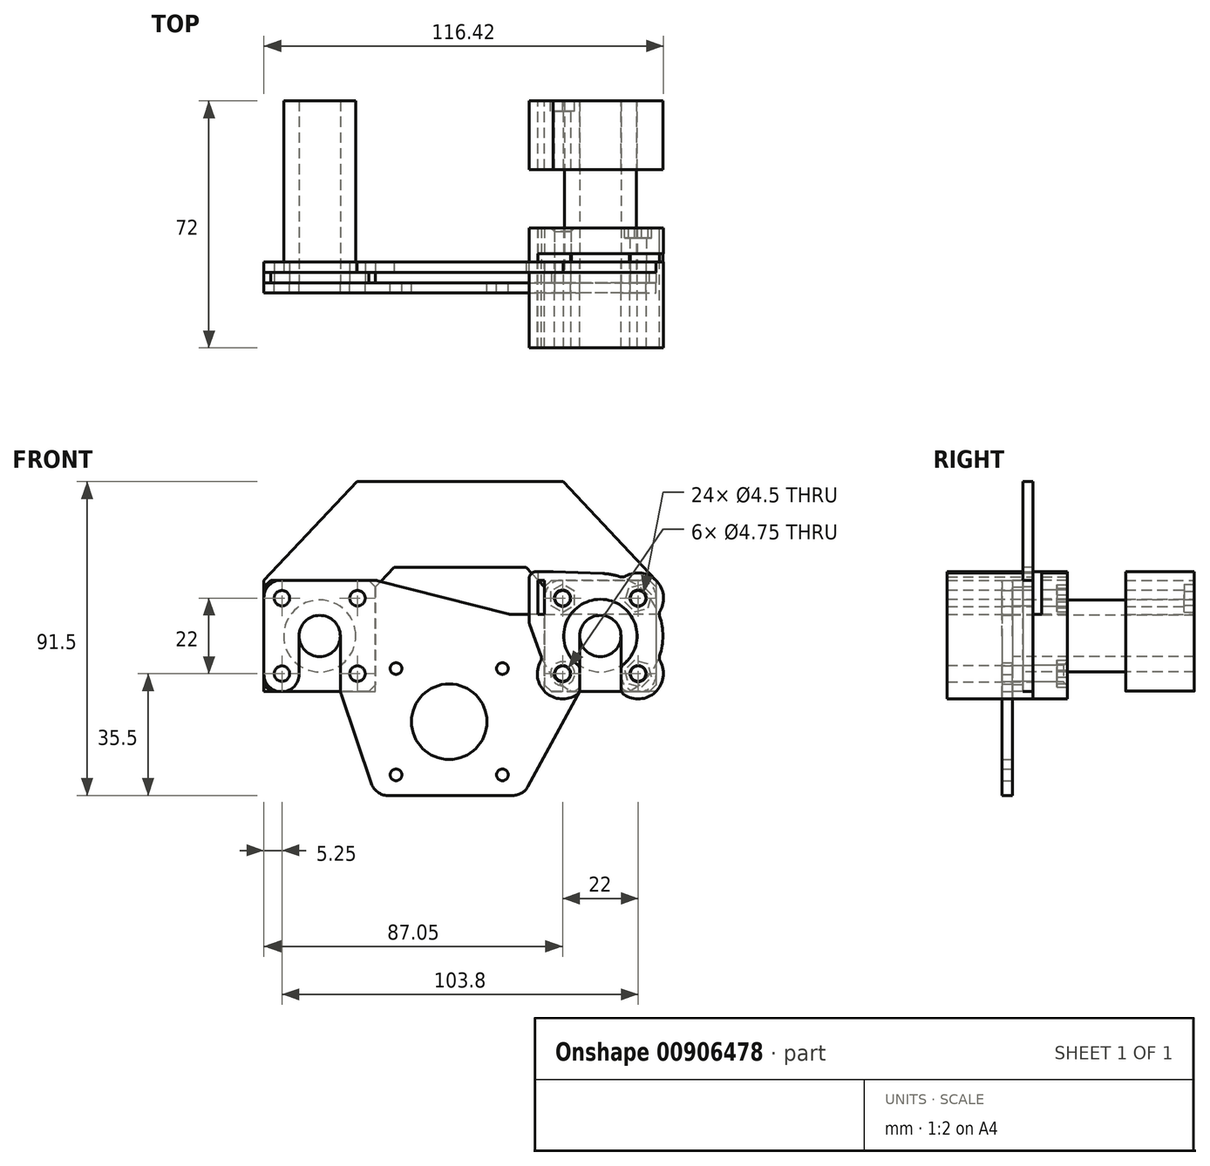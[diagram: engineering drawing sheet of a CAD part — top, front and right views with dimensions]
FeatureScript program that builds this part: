
annotation { "Feature Type Name" : "Feature", "Feature Type Description" : "" }
export const myFeature = defineFeature(function(context is Context, id is Id, definition is map)
    precondition{}
    {
        {
            var Q0;
            Q0=qCreatedBy(makeId("Front.planeOp"),FACE);
            var sketch = newSketch(context, id + "F0", { "sketchPlane" : qUnion([Q0])});
            skLineSegment(sketch, "E0", {"start": v(0, 0) * mm, "end": v(0, 38.28) * mm, "construction": true});
            skLineSegment(sketch, "E1", {"start": v(-57.15, 16.25) * mm, "end": v(-57.15, -16.25) * mm});
            skLineSegment(sketch, "E2", {"start": v(-57.15, -16.25) * mm, "end": v(-46.9, -16.25) * mm});
            skArc(sketch, "E3", {"start": v(-34.9, 0) * mm, "mid": v(-40.9, 6) * mm, "end": v(-46.9, 0) * mm});
            skLineSegment(sketch, "E4.bottom", {"start": v(-29.9, 11) * mm, "end": v(-51.9, 11) * mm, "construction": true});
            skLineSegment(sketch, "E4.top", {"start": v(-29.9, -11) * mm, "end": v(-51.9, -11) * mm, "construction": true});
            skLineSegment(sketch, "E4.left", {"start": v(-29.9, 11) * mm, "end": v(-29.9, -11) * mm, "construction": true});
            skLineSegment(sketch, "E4.right", {"start": v(-51.9, 11) * mm, "end": v(-51.9, -11) * mm, "construction": true});
            skCircle(sketch, "E5", {"center": v(-29.9, 11) * mm, "radius": 2.25 * mm});
            skCircle(sketch, "E6", {"center": v(-29.9, -11) * mm, "radius": 2.25 * mm});
            skCircle(sketch, "E7", {"center": v(-51.9, -11) * mm, "radius": 2.25 * mm});
            skCircle(sketch, "E8", {"center": v(-51.9, 11) * mm, "radius": 2.25 * mm});
            skLineSegment(sketch, "E9.bottom", {"start": v(-57.15, 16.25) * mm, "end": v(-24.65, 16.25) * mm, "construction": true});
            skLineSegment(sketch, "E9.top", {"start": v(-57.15, -16.25) * mm, "end": v(-24.65, -16.25) * mm, "construction": true});
            skLineSegment(sketch, "E9.left", {"start": v(-57.15, 16.25) * mm, "end": v(-57.15, -16.25) * mm, "construction": true});
            skLineSegment(sketch, "E9.right", {"start": v(-24.65, 16.25) * mm, "end": v(-24.65, -16.25) * mm, "construction": true});
            skLineSegment(sketch, "E10", {"start": v(-46.9, 0) * mm, "end": v(-46.9, -16.25) * mm});
            skLineSegment(sketch, "E11", {"start": v(-40.9, 0) * mm, "end": v(-40.9, -16.25) * mm, "construction": true});
            skLineSegment(sketch, "E12.MirrorCS", {"start": v(-34.9, 0) * mm, "end": v(-34.9, -16.25) * mm});
            skCircle(sketch, "E13", {"center": v(-3.15, -25) * mm, "radius": 11 * mm});
            skLineSegment(sketch, "E14.bottom", {"start": v(12.35, -9.5) * mm, "end": v(-18.65, -9.5) * mm, "construction": true});
            skLineSegment(sketch, "E14.top", {"start": v(12.35, -40.5) * mm, "end": v(-18.65, -40.5) * mm, "construction": true});
            skLineSegment(sketch, "E14.left", {"start": v(12.35, -9.5) * mm, "end": v(12.35, -40.5) * mm, "construction": true});
            skLineSegment(sketch, "E14.right", {"start": v(-18.65, -9.5) * mm, "end": v(-18.65, -40.5) * mm, "construction": true});
            skCircle(sketch, "E15", {"center": v(-18.65, -9.5) * mm, "radius": 1.7 * mm});
            skCircle(sketch, "E16", {"center": v(12.35, -9.5) * mm, "radius": 1.7 * mm});
            skCircle(sketch, "E17", {"center": v(12.35, -40.5) * mm, "radius": 1.7 * mm});
            skCircle(sketch, "E18", {"center": v(-18.65, -40.5) * mm, "radius": 1.7 * mm});
            skLineSegment(sketch, "E19.bottom", {"start": v(18.35, -3.5) * mm, "end": v(-24.65, -3.5) * mm, "construction": true});
            skLineSegment(sketch, "E19.top", {"start": v(18.35, -46.5) * mm, "end": v(-24.65, -46.5) * mm, "construction": true});
            skLineSegment(sketch, "E19.left", {"start": v(18.35, -3.5) * mm, "end": v(18.35, -46.5) * mm, "construction": true});
            skLineSegment(sketch, "E19.right", {"start": v(-24.65, -3.5) * mm, "end": v(-24.65, -46.5) * mm, "construction": true});
            skCircle(sketch, "E20.MirrorC", {"center": v(51.9, 11) * mm, "radius": 2.25 * mm});
            skCircle(sketch, "E21.MirrorC", {"center": v(29.9, 11) * mm, "radius": 2.25 * mm});
            skCircle(sketch, "E22.MirrorC", {"center": v(29.9, -11) * mm, "radius": 2.25 * mm});
            skCircle(sketch, "E23.MirrorC", {"center": v(51.9, -11) * mm, "radius": 2.25 * mm});
            skLineSegment(sketch, "E24.MirrorCS", {"start": v(46.9, 0) * mm, "end": v(46.9, -16.25) * mm});
            skLineSegment(sketch, "E25.MirrorCS", {"start": v(34.9, 0) * mm, "end": v(34.9, -16.25) * mm});
            skArc(sketch, "E26.MirrorCS", {"start": v(34.9, 0) * mm, "mid": v(40.9, 6) * mm, "end": v(46.9, 0) * mm});
            skLineSegment(sketch, "E27.MirrorCS", {"start": v(57.15, 16.25) * mm, "end": v(24.65, 16.25) * mm, "construction": true});
            skLineSegment(sketch, "E28.MirrorCS", {"start": v(24.65, 16.25) * mm, "end": v(24.65, -16.25) * mm, "construction": true});
            skLineSegment(sketch, "E29.MirrorCS", {"start": v(57.15, -16.25) * mm, "end": v(24.65, -16.25) * mm, "construction": true});
            skLineSegment(sketch, "E30.MirrorCS", {"start": v(57.15, 16.25) * mm, "end": v(57.15, -16.25) * mm, "construction": true});
            skLineSegment(sketch, "E31", {"start": v(-34.9, -16.25) * mm, "end": v(-24.65, -46.5) * mm});
            skLineSegment(sketch, "E32", {"start": v(18.35, -46.5) * mm, "end": v(-24.65, -46.5) * mm});
            skLineSegment(sketch, "E33", {"start": v(18.35, -46.5) * mm, "end": v(34.9, -16.25) * mm});
            skLineSegment(sketch, "E34", {"start": v(46.9, -16.25) * mm, "end": v(57.15, -16.25) * mm});
            skLineSegment(sketch, "E35", {"start": v(57.15, 16.25) * mm, "end": v(57.15, -16.25) * mm});
            skLineSegment(sketch, "E36", {"start": v(57.15, 16.25) * mm, "end": v(24.65, 16.25) * mm});
            skLineSegment(sketch, "E37", {"start": v(24.65, 16.25) * mm, "end": v(24.65, 6.25) * mm});
            skLineSegment(sketch, "E38", {"start": v(24.65, 6.25) * mm, "end": v(14.65, 6.25) * mm});
            skLineSegment(sketch, "E39", {"start": v(14.65, 6.25) * mm, "end": v(-24.65, 16.25) * mm});
            skLineSegment(sketch, "E40", {"start": v(-57.15, 16.25) * mm, "end": v(-24.65, 16.25) * mm});
            skSolve(sketch);
        }
        {
            var Q0;
            Q0 = qSketchRegion(id + "F0", true);
            extrude(context, id + "F1", {"entities" : qUnion([Q0]), "depth" : 3 * mm, "offsetDistance" : 25 * mm});
        }
        {
            var Q0;
            Q0=makeQuery(id+"F1.opExtrude","SWEPT_EDGE",EDGE,{"disambiguationData":[OSD([sQuery(id+"F0.wireOp",EDGE,"E1"),sQuery(id+"F0.wireOp",EDGE,"E2")])]});
            var Q1;
            Q1=makeQuery(id+"F1.opExtrude","SWEPT_EDGE",EDGE,{"disambiguationData":[OSD([sQuery(id+"F0.wireOp",EDGE,"E1"),sQuery(id+"F0.wireOp",EDGE,"E40")])]});
            var Q2;
            Q2=makeQuery(id+"F1.opExtrude","SWEPT_EDGE",EDGE,{"disambiguationData":[OSD([sQuery(id+"F0.wireOp",EDGE,"E2"),sQuery(id+"F0.wireOp",EDGE,"E10")])]});
            var Q3;
            Q3=makeQuery(id+"F1.opExtrude","SWEPT_EDGE",EDGE,{"disambiguationData":[OSD([sQuery(id+"F0.wireOp",EDGE,"E12.MirrorCS"),sQuery(id+"F0.wireOp",EDGE,"E31")])]});
            var Q4;
            Q4=makeQuery(id+"F1.opExtrude","SWEPT_EDGE",EDGE,{"disambiguationData":[OSD([sQuery(id+"F0.wireOp",EDGE,"E31"),sQuery(id+"F0.wireOp",EDGE,"E32")])]});
            var Q5;
            Q5=makeQuery(id+"F1.opExtrude","SWEPT_EDGE",EDGE,{"disambiguationData":[OSD([sQuery(id+"F0.wireOp",EDGE,"E32"),sQuery(id+"F0.wireOp",EDGE,"E33")])]});
            var Q6;
            Q6=makeQuery(id+"F1.opExtrude","SWEPT_EDGE",EDGE,{"disambiguationData":[OSD([sQuery(id+"F0.wireOp",EDGE,"E25.MirrorCS"),sQuery(id+"F0.wireOp",EDGE,"E33")])]});
            var Q7;
            Q7=makeQuery(id+"F1.opExtrude","SWEPT_EDGE",EDGE,{"disambiguationData":[OSD([sQuery(id+"F0.wireOp",EDGE,"E24.MirrorCS"),sQuery(id+"F0.wireOp",EDGE,"E34")])]});
            var Q8;
            Q8=makeQuery(id+"F1.opExtrude","SWEPT_EDGE",EDGE,{"disambiguationData":[OSD([sQuery(id+"F0.wireOp",EDGE,"E34"),sQuery(id+"F0.wireOp",EDGE,"E35")])]});
            var Q9;
            Q9=makeQuery(id+"F1.opExtrude","SWEPT_EDGE",EDGE,{"disambiguationData":[OSD([sQuery(id+"F0.wireOp",EDGE,"E35"),sQuery(id+"F0.wireOp",EDGE,"E36")])]});
            var Q10;
            Q10=makeQuery(id+"F1.opExtrude","SWEPT_EDGE",EDGE,{"disambiguationData":[OSD([sQuery(id+"F0.wireOp",EDGE,"E36"),sQuery(id+"F0.wireOp",EDGE,"E37")])]});
            var Q11;
            Q11=makeQuery(id+"F1.opExtrude","SWEPT_EDGE",EDGE,{"disambiguationData":[OSD([sQuery(id+"F0.wireOp",EDGE,"E38"),sQuery(id+"F0.wireOp",EDGE,"E39")])]});
            var Q12;
            Q12=makeQuery(id+"F1.opExtrude","SWEPT_EDGE",EDGE,{"disambiguationData":[OSD([sQuery(id+"F0.wireOp",EDGE,"E39"),sQuery(id+"F0.wireOp",EDGE,"E40")])]});
            fillet(context, id + "F2", {"entities" : qUnion([Q0, Q1, Q2, Q3, Q4, Q5, Q6, Q7, Q8, Q9, Q10, Q11, Q12]), "radius" : 5 * mm, "tangentPropagation" : true, "allowEdgeOverflow" : false});
        }
        {
            var Q0;
            Q0=makeQuery(id+"F1.opExtrude","CAP_FACE",FACE,{"disambiguationData":[OSD([sQuery(id+"F0.wireOp",EDGE,"E1"),sQuery(id+"F0.wireOp",EDGE,"E2"),sQuery(id+"F0.wireOp",EDGE,"E3"),sQuery(id+"F0.wireOp",EDGE,"E5"),sQuery(id+"F0.wireOp",EDGE,"E6"),sQuery(id+"F0.wireOp",EDGE,"E7"),sQuery(id+"F0.wireOp",EDGE,"E8"),sQuery(id+"F0.wireOp",EDGE,"E10"),sQuery(id+"F0.wireOp",EDGE,"E12.MirrorCS"),sQuery(id+"F0.wireOp",EDGE,"E13"),sQuery(id+"F0.wireOp",EDGE,"E15"),sQuery(id+"F0.wireOp",EDGE,"E16"),sQuery(id+"F0.wireOp",EDGE,"E17"),sQuery(id+"F0.wireOp",EDGE,"E18"),sQuery(id+"F0.wireOp",EDGE,"E20.MirrorC"),sQuery(id+"F0.wireOp",EDGE,"E21.MirrorC"),sQuery(id+"F0.wireOp",EDGE,"E22.MirrorC"),sQuery(id+"F0.wireOp",EDGE,"E23.MirrorC"),sQuery(id+"F0.wireOp",EDGE,"E24.MirrorCS"),sQuery(id+"F0.wireOp",EDGE,"E25.MirrorCS"),sQuery(id+"F0.wireOp",EDGE,"E26.MirrorCS"),sQuery(id+"F0.wireOp",EDGE,"E31"),sQuery(id+"F0.wireOp",EDGE,"E32"),sQuery(id+"F0.wireOp",EDGE,"E33"),sQuery(id+"F0.wireOp",EDGE,"E34"),sQuery(id+"F0.wireOp",EDGE,"E35"),sQuery(id+"F0.wireOp",EDGE,"E36"),sQuery(id+"F0.wireOp",EDGE,"E37"),sQuery(id+"F0.wireOp",EDGE,"E38"),sQuery(id+"F0.wireOp",EDGE,"E39"),sQuery(id+"F0.wireOp",EDGE,"E40")])],"isStart":true});
            var sketch = newSketch(context, id + "F3", { "sketchPlane" : qUnion([Q0])});
            skLineSegment(sketch, "E41.bottom", {"start": v(-24.65, 16.25) * mm, "end": v(-57.15, 16.25) * mm});
            skLineSegment(sketch, "E41.top", {"start": v(-24.65, -16.25) * mm, "end": v(-57.15, -16.25) * mm});
            skLineSegment(sketch, "E41.left", {"start": v(-24.65, 16.25) * mm, "end": v(-24.65, -16.25) * mm});
            skLineSegment(sketch, "E41.right", {"start": v(-57.15, 16.25) * mm, "end": v(-57.15, -16.25) * mm});
            skPoint(sketch, "E41.middle", {"position": v(-40.9, 0) * mm});
            skCircle(sketch, "E42.0", {"center": v(-51.9, 11) * mm, "radius": 2.25 * mm});
            skCircle(sketch, "E43.0", {"center": v(-29.9, 11) * mm, "radius": 2.25 * mm});
            skCircle(sketch, "E44.0", {"center": v(-29.9, -11) * mm, "radius": 2.25 * mm});
            skCircle(sketch, "E45.0", {"center": v(-51.9, -11) * mm, "radius": 2.25 * mm});
            skCircle(sketch, "E46", {"center": v(-40.9, 0) * mm, "radius": 6 * mm});
            skSolve(sketch);
        }
        {
            var Q0;
            Q0 = qSketchRegion(id + "F3", true);
            extrude(context, id + "F4", {"entities" : qUnion([Q0]), "depth" : 3 * mm, "offsetDistance" : 25 * mm});
        }
        {
            var Q0;
            Q0=makeQuery(id+"F4.opExtrude","CAP_FACE",FACE,{"disambiguationData":[OSD([sQuery(id+"F3.wireOp",EDGE,"E41.bottom"),sQuery(id+"F3.wireOp",EDGE,"E41.top"),sQuery(id+"F3.wireOp",EDGE,"E41.left"),sQuery(id+"F3.wireOp",EDGE,"E41.right"),sQuery(id+"F3.wireOp",EDGE,"E42.0"),sQuery(id+"F3.wireOp",EDGE,"E43.0"),sQuery(id+"F3.wireOp",EDGE,"E44.0"),sQuery(id+"F3.wireOp",EDGE,"E45.0"),sQuery(id+"F3.wireOp",EDGE,"E46")])],"isStart":false});
            var sketch = newSketch(context, id + "F5", { "sketchPlane" : qUnion([Q0])});
            skCircle(sketch, "E47.0", {"center": v(-40.9, 0) * mm, "radius": 6 * mm});
            skCircle(sketch, "E48", {"center": v(-40.9, 0) * mm, "radius": 10.5 * mm});
            skSolve(sketch);
        }
        {
            var Q0;
            Q0 = qSketchRegion(id + "F5", true);
            extrude(context, id + "F6", {"entities" : qUnion([Q0]), "operationType" : NewBodyOperationType.ADD, "depth" : 50 * mm, "offsetDistance" : 25 * mm});
        }
        {
            var Q0;
            Q0=makeQuery(id+"F4.opExtrude","SWEPT_EDGE",EDGE,{"disambiguationData":[OSD([sQuery(id+"F3.wireOp",EDGE,"E41.bottom"),sQuery(id+"F3.wireOp",EDGE,"E41.right")])]});
            var Q1;
            Q1=makeQuery(id+"F4.opExtrude","SWEPT_EDGE",EDGE,{"disambiguationData":[OSD([sQuery(id+"F3.wireOp",EDGE,"E41.bottom"),sQuery(id+"F3.wireOp",EDGE,"E41.left")])]});
            var Q2;
            Q2=makeQuery(id+"F4.opExtrude","SWEPT_EDGE",EDGE,{"disambiguationData":[OSD([sQuery(id+"F3.wireOp",EDGE,"E41.top"),sQuery(id+"F3.wireOp",EDGE,"E41.left")])]});
            var Q3;
            Q3=makeQuery(id+"F4.opExtrude","SWEPT_EDGE",EDGE,{"disambiguationData":[OSD([sQuery(id+"F3.wireOp",EDGE,"E41.top"),sQuery(id+"F3.wireOp",EDGE,"E41.right")])]});
            chamfer(context, id + "F7", {"entities" : qUnion([Q0, Q1, Q2, Q3]), "width" : 2 * mm, "tangentPropagation" : true});
        }
        {
            var Q0;
            Q0=makeQuery(id+"F4.opExtrude","SWEPT_BODY",BODY,{"disambiguationData":[OSD([sQuery(id+"F3.wireOp",EDGE,"E41.bottom"),sQuery(id+"F3.wireOp",EDGE,"E41.top"),sQuery(id+"F3.wireOp",EDGE,"E41.left"),sQuery(id+"F3.wireOp",EDGE,"E41.right"),sQuery(id+"F3.wireOp",EDGE,"E42.0"),sQuery(id+"F3.wireOp",EDGE,"E43.0"),sQuery(id+"F3.wireOp",EDGE,"E44.0"),sQuery(id+"F3.wireOp",EDGE,"E45.0"),sQuery(id+"F3.wireOp",EDGE,"E46")])]});
            var Q1;
            Q1=qCreatedBy(makeId("Right.planeOp"),FACE);
            mirror(context, id + "F8", {"entities" : qUnion([Q0]), "mirrorPlane" : qUnion([Q1])});
        }
        {
            var Q0;
            Q0=makeQuery(id+"F4.opExtrude","CAP_FACE",FACE,{"disambiguationData":[OSD([sQuery(id+"F3.wireOp",EDGE,"E41.bottom"),sQuery(id+"F3.wireOp",EDGE,"E41.top"),sQuery(id+"F3.wireOp",EDGE,"E41.left"),sQuery(id+"F3.wireOp",EDGE,"E41.right"),sQuery(id+"F3.wireOp",EDGE,"E42.0"),sQuery(id+"F3.wireOp",EDGE,"E43.0"),sQuery(id+"F3.wireOp",EDGE,"E44.0"),sQuery(id+"F3.wireOp",EDGE,"E45.0"),sQuery(id+"F3.wireOp",EDGE,"E46")])],"isStart":false});
            cPlane(context, id + "F9", {"entities" : qUnion([Q0]), "cplaneType" : CPlaneType.OFFSET, "offset" : 3 * mm, "width" : 150 * mm, "height" : 150 * mm});
        }
        {
            var Q0;
            Q0=qCreatedBy(id+"F9.planeOp",FACE);
            var sketch = newSketch(context, id + "F10", { "sketchPlane" : qUnion([Q0])});
            skCircle(sketch, "E49.0", {"center": v(-40.9, 0) * mm, "radius": 10.5 * mm, "construction": true});
            skArc(sketch, "E50", {"start": v(-34.9, -8.86) * mm, "mid": v(-40.9, 10.7) * mm, "end": v(-46.9, -8.86) * mm});
            skLineSegment(sketch, "E51", {"start": v(-40.9, 0) * mm, "end": v(-40.9, -10.7) * mm, "construction": true});
            skLineSegment(sketch, "E52", {"start": v(-34.9, -8.86) * mm, "end": v(-34.9, -16.42) * mm});
            skLineSegment(sketch, "E53.MirrorCS", {"start": v(-46.9, -8.86) * mm, "end": v(-46.9, -16.42) * mm});
            skLineSegment(sketch, "E54.bottom", {"start": v(-22.65, 16.25) * mm, "end": v(-24.65, 16.25) * mm});
            skLineSegment(sketch, "E54.top", {"start": v(-22.65, 6.25) * mm, "end": v(-24.65, 6.25) * mm});
            skLineSegment(sketch, "E54.left", {"start": v(-22.65, 16.25) * mm, "end": v(-22.65, 6.25) * mm});
            skLineSegment(sketch, "E54.right", {"start": v(-24.65, 16.25) * mm, "end": v(-24.65, 6.25) * mm});
            skPoint(sketch, "E54.middle", {"position": v(-23.65, 11.25) * mm});
            skArc(sketch, "E55", {"start": v(-23.95, -6.64) * mm, "mid": v(-23.88, -6.44) * mm, "end": v(-23.8, -6.25) * mm});
            skLineSegment(sketch, "E56", {"start": v(-23.8, -6.25) * mm, "end": v(-20.15, 3.75) * mm});
            skLineSegment(sketch, "E57", {"start": v(-20.15, 3.75) * mm, "end": v(-20.15, 18.75) * mm});
            skLineSegment(sketch, "E58", {"start": v(-20.15, 18.75) * mm, "end": v(-27.15, 18.75) * mm});
            skLineSegment(sketch, "E59", {"start": v(-27.15, 18.75) * mm, "end": v(-41.6, 18.19) * mm});
            skLineSegment(sketch, "E60", {"start": v(-22.65, 16.25) * mm, "end": v(-22.65, 18.75) * mm, "construction": true});
            skLineSegment(sketch, "E61", {"start": v(-22.65, 16.25) * mm, "end": v(-20.15, 16.25) * mm, "construction": true});
            skLineSegment(sketch, "E62", {"start": v(-27.15, 18.75) * mm, "end": v(-27.15, 16.25) * mm, "construction": true});
            skArc(sketch, "E63.trimOffspring", {"start": v(-41.6, 18.19) * mm, "mid": v(-44.63, 17.81) * mm, "end": v(-47.54, 16.95) * mm});
            skLineSegment(sketch, "E64", {"start": v(-22.65, 6.25) * mm, "end": v(-22.65, 3.75) * mm, "construction": true});
            skLineSegment(sketch, "E65", {"start": v(-22.65, 3.75) * mm, "end": v(-20.15, 3.75) * mm, "construction": true});
            skCircle(sketch, "E66.0", {"center": v(-51.9, 11) * mm, "radius": 2.38 * mm});
            skCircle(sketch, "E67.0", {"center": v(-29.9, 11) * mm, "radius": 2.38 * mm});
            skCircle(sketch, "E68.0", {"center": v(-29.9, -11) * mm, "radius": 2.38 * mm});
            skCircle(sketch, "E69.0", {"center": v(-51.9, -11) * mm, "radius": 2.38 * mm});
            skArc(sketch, "E70", {"start": v(-47.54, 16.95) * mm, "mid": v(-57.11, 16.21) * mm, "end": v(-57.85, 6.64) * mm});
            skArc(sketch, "E71", {"start": v(-57.85, -6.64) * mm, "mid": v(-56.81, -16.5) * mm, "end": v(-46.9, -16.42) * mm});
            skArc(sketch, "E72", {"start": v(-34.9, -16.42) * mm, "mid": v(-24.99, -16.5) * mm, "end": v(-23.95, -6.64) * mm});
            skArc(sketch, "E73.trimOffspring", {"start": v(-57.85, 6.64) * mm, "mid": v(-59.1, 0) * mm, "end": v(-57.85, -6.64) * mm});
            skPoint(sketch, "E74.orphan", {"position": v(-46.9, -17.18) * mm});
            skPoint(sketch, "E75.orphan", {"position": v(-34.9, -17.18) * mm});
            skLineSegment(sketch, "E76", {"start": v(-27.15, 16.25) * mm, "end": v(-24.65, 16.25) * mm, "construction": true});
            skSolve(sketch);
        }
        {
            var Q0;
            Q0 = qSketchRegion(id + "F10", true);
            extrude(context, id + "F11", {"entities" : qUnion([Q0]), "depth" : 10 * mm, "offsetDistance" : 25 * mm});
        }
        {
            var Q0;
            Q0=makeQuery(id+"F11.opExtrude","SWEPT_FACE",FACE,{"disambiguationData":[OSD([sQuery(id+"F10.wireOp",EDGE,"E54.left")])]});
            var sketch = newSketch(context, id + "F12", { "sketchPlane" : qUnion([Q0])});
            skLineSegment(sketch, "E77.bottom", {"start": v(6, 6.25) * mm, "end": v(8.5, 6.25) * mm});
            skLineSegment(sketch, "E77.top", {"start": v(6, 18.75) * mm, "end": v(8.5, 18.75) * mm});
            skLineSegment(sketch, "E77.left", {"start": v(6, 6.25) * mm, "end": v(6, 18.75) * mm});
            skLineSegment(sketch, "E77.right", {"start": v(8.5, 6.25) * mm, "end": v(8.5, 18.75) * mm});
            skSolve(sketch);
        }
        {
            var Q0;
            Q0=makeQuery(id+"F6.opExtrude","CAP_FACE",FACE,{"disambiguationData":[OSD([sQuery(id+"F5.wireOp",EDGE,"E47.0"),sQuery(id+"F5.wireOp",EDGE,"E48")])],"isStart":false});
            var sketch = newSketch(context, id + "F13", { "sketchPlane" : qUnion([Q0])});
            skArc(sketch, "E78.0.0", {"start": v(-41.6, 18.19) * mm, "mid": v(-44.63, 17.81) * mm, "end": v(-47.54, 16.95) * mm});
            skArc(sketch, "E78.0.2", {"start": v(-57.85, 6.64) * mm, "mid": v(-59.1, 0) * mm, "end": v(-57.85, -6.64) * mm});
            skArc(sketch, "E78.0.3", {"start": v(-47.54, -16.95) * mm, "mid": v(-47.21, -16.7) * mm, "end": v(-46.9, -16.42) * mm});
            skLineSegment(sketch, "E78.0.4", {"start": v(-46.9, -16.42) * mm, "end": v(-46.9, -8.86) * mm});
            skArc(sketch, "E78.0.5", {"start": v(-46.9, -8.86) * mm, "mid": v(-40.9, 10.7) * mm, "end": v(-34.9, -8.86) * mm});
            skLineSegment(sketch, "E78.0.6", {"start": v(-34.9, -8.86) * mm, "end": v(-34.9, -16.42) * mm});
            skArc(sketch, "E78.0.7", {"start": v(-34.9, -16.42) * mm, "mid": v(-34.59, -16.7) * mm, "end": v(-34.26, -16.95) * mm});
            skArc(sketch, "E78.0.8", {"start": v(-23.95, -6.64) * mm, "mid": v(-23.88, -6.44) * mm, "end": v(-23.8, -6.25) * mm});
            skLineSegment(sketch, "E78.0.9", {"start": v(-23.8, -6.25) * mm, "end": v(-20.15, 3.75) * mm});
            skLineSegment(sketch, "E78.0.10", {"start": v(-20.15, 3.75) * mm, "end": v(-20.15, 18.75) * mm});
            skLineSegment(sketch, "E78.0.11", {"start": v(-20.15, 18.75) * mm, "end": v(-27.15, 18.75) * mm});
            skLineSegment(sketch, "E78.0.12", {"start": v(-27.15, 18.75) * mm, "end": v(-41.6, 18.19) * mm});
            skCircle(sketch, "E79.0", {"center": v(-29.9, 11) * mm, "radius": 2.37 * mm});
            skLineSegment(sketch, "E80.0", {"start": v(-24.65, 16.25) * mm, "end": v(-24.65, 6.25) * mm});
            skLineSegment(sketch, "E81.0", {"start": v(-22.65, 16.25) * mm, "end": v(-24.65, 16.25) * mm});
            skLineSegment(sketch, "E82.0", {"start": v(-22.65, 16.25) * mm, "end": v(-22.65, 6.25) * mm});
            skLineSegment(sketch, "E83.0", {"start": v(-22.65, 6.25) * mm, "end": v(-24.65, 6.25) * mm});
            skArc(sketch, "E84", {"start": v(-34.26, -16.95) * mm, "mid": v(-27.89, -12.72) * mm, "end": v(-23.8, -6.25) * mm});
            skArc(sketch, "E85.trimOffspring", {"start": v(-41.6, 18.19) * mm, "mid": v(-58.85, 3.03) * mm, "end": v(-47.54, -16.95) * mm});
            skSolve(sketch);
        }
        {
            var Q0;
            Q0 = qSketchRegion(id + "F13", true);
            extrude(context, id + "F14", {"entities" : qUnion([Q0]), "oppositeDirection" : true, "depth" : 20 * mm, "offsetDistance" : 25 * mm});
        }
        {
            var Q0;
            Q0 = qSketchRegion(id + "F12", true);
            extrude(context, id + "F15", {"entities" : qUnion([Q0]), "operationType" : NewBodyOperationType.REMOVE, "endBound" : BoundingType.THROUGH_ALL, "depth" : 25 * mm, "offsetDistance" : 25 * mm});
        }
        {
            var Q0;
            Q0=makeQuery(id+"F11.opExtrude","CAP_FACE",FACE,{"disambiguationData":[OSD([sQuery(id+"F10.wireOp",EDGE,"E50"),sQuery(id+"F10.wireOp",EDGE,"E52"),sQuery(id+"F10.wireOp",EDGE,"E53.MirrorCS"),sQuery(id+"F10.wireOp",EDGE,"E54.bottom"),sQuery(id+"F10.wireOp",EDGE,"E54.top"),sQuery(id+"F10.wireOp",EDGE,"E54.left"),sQuery(id+"F10.wireOp",EDGE,"E54.right"),sQuery(id+"F10.wireOp",EDGE,"E55"),sQuery(id+"F10.wireOp",EDGE,"E56"),sQuery(id+"F10.wireOp",EDGE,"E57"),sQuery(id+"F10.wireOp",EDGE,"E58"),sQuery(id+"F10.wireOp",EDGE,"E59"),sQuery(id+"F10.wireOp",EDGE,"E63.trimOffspring"),sQuery(id+"F10.wireOp",EDGE,"E66.0"),sQuery(id+"F10.wireOp",EDGE,"E67.0"),sQuery(id+"F10.wireOp",EDGE,"E68.0"),sQuery(id+"F10.wireOp",EDGE,"E69.0"),sQuery(id+"F10.wireOp",EDGE,"E70"),sQuery(id+"F10.wireOp",EDGE,"E71"),sQuery(id+"F10.wireOp",EDGE,"E72"),sQuery(id+"F10.wireOp",EDGE,"E73.trimOffspring")])],"isStart":false});
            var sketch = newSketch(context, id + "F16", { "sketchPlane" : qUnion([Q0])});
            skCircle(sketch, "E86.cCircle", {"center": v(-51.9, 11) * mm, "radius": 3.5 * mm, "construction": true});
            skLineSegment(sketch, "E86.0", {"start": v(-49.04, 13.86) * mm, "end": v(-48, 9.95) * mm});
            skLineSegment(sketch, "E86.1", {"start": v(-48, 9.95) * mm, "end": v(-50.85, 7.1) * mm});
            skLineSegment(sketch, "E86.2", {"start": v(-50.85, 7.1) * mm, "end": v(-54.76, 8.14) * mm});
            skLineSegment(sketch, "E86.3", {"start": v(-54.76, 8.14) * mm, "end": v(-55.8, 12.05) * mm});
            skLineSegment(sketch, "E86.4", {"start": v(-55.8, 12.05) * mm, "end": v(-52.95, 14.9) * mm});
            skLineSegment(sketch, "E86.5", {"start": v(-52.95, 14.9) * mm, "end": v(-49.04, 13.86) * mm});
            skPoint(sketch, "E86.0.midPoint", {"position": v(-48.52, 11.9) * mm});
            skCircle(sketch, "E87.cCircle", {"center": v(-51.9, -11) * mm, "radius": 3.5 * mm, "construction": true});
            skLineSegment(sketch, "E87.0", {"start": v(-54.76, -8.14) * mm, "end": v(-50.85, -7.1) * mm});
            skLineSegment(sketch, "E87.1", {"start": v(-50.85, -7.1) * mm, "end": v(-48, -9.95) * mm});
            skLineSegment(sketch, "E87.2", {"start": v(-48, -9.95) * mm, "end": v(-49.04, -13.86) * mm});
            skLineSegment(sketch, "E87.3", {"start": v(-49.04, -13.86) * mm, "end": v(-52.95, -14.9) * mm});
            skLineSegment(sketch, "E87.4", {"start": v(-52.95, -14.9) * mm, "end": v(-55.8, -12.05) * mm});
            skLineSegment(sketch, "E87.5", {"start": v(-55.8, -12.05) * mm, "end": v(-54.76, -8.14) * mm});
            skPoint(sketch, "E87.0.midPoint", {"position": v(-52.8, -7.62) * mm});
            skCircle(sketch, "E88.cCircle", {"center": v(-29.9, -11) * mm, "radius": 3.5 * mm, "construction": true});
            skLineSegment(sketch, "E88.0", {"start": v(-27.04, -8.14) * mm, "end": v(-26, -12.05) * mm, "construction": true});
            skLineSegment(sketch, "E88.1", {"start": v(-26, -12.05) * mm, "end": v(-28.85, -14.9) * mm, "construction": true});
            skLineSegment(sketch, "E88.2", {"start": v(-28.85, -14.9) * mm, "end": v(-32.76, -13.86) * mm, "construction": true});
            skLineSegment(sketch, "E88.3", {"start": v(-32.76, -13.86) * mm, "end": v(-33.8, -9.95) * mm, "construction": true});
            skLineSegment(sketch, "E88.4", {"start": v(-33.8, -9.95) * mm, "end": v(-30.95, -7.1) * mm, "construction": true});
            skLineSegment(sketch, "E88.5", {"start": v(-30.95, -7.1) * mm, "end": v(-27.04, -8.14) * mm, "construction": true});
            skPoint(sketch, "E88.0.midPoint", {"position": v(-26.52, -10.1) * mm});
            skLineSegment(sketch, "E89", {"start": v(-49.43, 8.53) * mm, "end": v(-32.37, -8.53) * mm, "construction": true});
            skSolve(sketch);
        }
        {
            var Q0;
            Q0 = qSketchRegion(id + "F16", true);
            extrude(context, id + "F17", {"entities" : qUnion([Q0]), "operationType" : NewBodyOperationType.REMOVE, "oppositeDirection" : true, "depth" : 3 * mm, "offsetDistance" : 25 * mm});
        }
        {
            var Q0;
            Q0=makeQuery(id+"F14.opExtrude","SWEPT_EDGE",EDGE,{"disambiguationData":[OSD([sQuery(id+"F13.wireOp",EDGE,"E78.0.3"),sQuery(id+"F13.wireOp",EDGE,"E78.0.4")])]});
            var Q1;
            Q1=makeQuery(id+"F11.opExtrude","SWEPT_EDGE",EDGE,{"disambiguationData":[OSD([sQuery(id+"F10.wireOp",EDGE,"E63.trimOffspring"),sQuery(id+"F10.wireOp",EDGE,"E70")])]});
            var Q2;
            Q2=makeQuery(id+"F11.opExtrude","SWEPT_EDGE",EDGE,{"disambiguationData":[OSD([sQuery(id+"F10.wireOp",EDGE,"E70"),sQuery(id+"F10.wireOp",EDGE,"E73.trimOffspring")])]});
            var Q3;
            Q3=makeQuery(id+"F11.opExtrude","SWEPT_EDGE",EDGE,{"disambiguationData":[OSD([sQuery(id+"F10.wireOp",EDGE,"E71"),sQuery(id+"F10.wireOp",EDGE,"E73.trimOffspring")])]});
            var Q4;
            Q4=makeQuery(id+"F11.opExtrude","SWEPT_EDGE",EDGE,{"disambiguationData":[OSD([sQuery(id+"F10.wireOp",EDGE,"E53.MirrorCS"),sQuery(id+"F10.wireOp",EDGE,"E71")])]});
            var Q5;
            Q5=makeQuery(id+"F11.opExtrude","SWEPT_EDGE",EDGE,{"disambiguationData":[OSD([sQuery(id+"F10.wireOp",EDGE,"E50"),sQuery(id+"F10.wireOp",EDGE,"E53.MirrorCS")])]});
            var Q6;
            Q6=makeQuery(id+"F11.opExtrude","SWEPT_EDGE",EDGE,{"disambiguationData":[OSD([sQuery(id+"F10.wireOp",EDGE,"E55"),sQuery(id+"F10.wireOp",EDGE,"E72")])]});
            var Q7;
            Q7=makeQuery(id+"F11.opExtrude","SWEPT_EDGE",EDGE,{"disambiguationData":[OSD([sQuery(id+"F10.wireOp",EDGE,"E56"),sQuery(id+"F10.wireOp",EDGE,"E57")])]});
            var Q8;
            Q8=makeQuery(id+"F11.opExtrude","SWEPT_EDGE",EDGE,{"disambiguationData":[OSD([sQuery(id+"F10.wireOp",EDGE,"E57"),sQuery(id+"F10.wireOp",EDGE,"E58")])]});
            var Q9;
            Q9=makeQuery(id+"F11.opExtrude","SWEPT_EDGE",EDGE,{"disambiguationData":[OSD([sQuery(id+"F10.wireOp",EDGE,"E58"),sQuery(id+"F10.wireOp",EDGE,"E59")])]});
            var Q10;
            Q10=makeQuery(id+"F11.opExtrude","SWEPT_EDGE",EDGE,{"disambiguationData":[OSD([sQuery(id+"F10.wireOp",EDGE,"E50"),sQuery(id+"F10.wireOp",EDGE,"E52")])]});
            var Q11;
            Q11=makeQuery(id+"F11.opExtrude","SWEPT_EDGE",EDGE,{"disambiguationData":[OSD([sQuery(id+"F10.wireOp",EDGE,"E52"),sQuery(id+"F10.wireOp",EDGE,"E72")])]});
            var Q12;
            Q12=makeQuery(id+"F14.opExtrude","SWEPT_EDGE",EDGE,{"disambiguationData":[OSD([sQuery(id+"F13.wireOp",EDGE,"E78.0.4"),sQuery(id+"F13.wireOp",EDGE,"E78.0.5")])]});
            var Q13;
            Q13=makeQuery(id+"F14.opExtrude","SWEPT_EDGE",EDGE,{"disambiguationData":[OSD([sQuery(id+"F13.wireOp",EDGE,"E78.0.7"),sQuery(id+"F13.wireOp",EDGE,"E84")])]});
            var Q14;
            Q14=makeQuery(id+"F14.opExtrude","SWEPT_EDGE",EDGE,{"disambiguationData":[OSD([sQuery(id+"F13.wireOp",EDGE,"E78.0.5"),sQuery(id+"F13.wireOp",EDGE,"E78.0.6")])]});
            var Q15;
            Q15=makeQuery(id+"F14.opExtrude","SWEPT_EDGE",EDGE,{"disambiguationData":[OSD([sQuery(id+"F13.wireOp",EDGE,"E78.0.9"),sQuery(id+"F13.wireOp",EDGE,"E78.0.10")])]});
            var Q16;
            Q16=makeQuery(id+"F14.opExtrude","SWEPT_EDGE",EDGE,{"disambiguationData":[OSD([sQuery(id+"F13.wireOp",EDGE,"E78.0.10"),sQuery(id+"F13.wireOp",EDGE,"E78.0.11")])]});
            fillet(context, id + "F18", {"entities" : qUnion([Q0, Q1, Q2, Q3, Q4, Q5, Q6, Q7, Q8, Q9, Q10, Q11, Q12, Q13, Q14, Q15, Q16]), "radius" : 2 * mm, "tangentPropagation" : true, "allowEdgeOverflow" : false});
        }
        {
            var Q0;
            Q0=makeQuery(id+"F4.opExtrude","CAP_FACE",FACE,{"disambiguationData":[OSD([sQuery(id+"F3.wireOp",EDGE,"E41.bottom"),sQuery(id+"F3.wireOp",EDGE,"E41.top"),sQuery(id+"F3.wireOp",EDGE,"E41.left"),sQuery(id+"F3.wireOp",EDGE,"E41.right"),sQuery(id+"F3.wireOp",EDGE,"E42.0"),sQuery(id+"F3.wireOp",EDGE,"E43.0"),sQuery(id+"F3.wireOp",EDGE,"E44.0"),sQuery(id+"F3.wireOp",EDGE,"E45.0"),sQuery(id+"F3.wireOp",EDGE,"E46")])],"isStart":false});
            var sketch = newSketch(context, id + "F19", { "sketchPlane" : qUnion([Q0])});
            skCircle(sketch, "E90.0", {"center": v(-51.9, 11) * mm, "radius": 2.25 * mm});
            skCircle(sketch, "E91.0", {"center": v(-29.9, 11) * mm, "radius": 2.25 * mm});
            skCircle(sketch, "E92.0", {"center": v(-51.9, -11) * mm, "radius": 2.25 * mm});
            skCircle(sketch, "E93.0", {"center": v(-29.9, -11) * mm, "radius": 2.25 * mm});
            skCircle(sketch, "E94.0", {"center": v(51.9, -11) * mm, "radius": 2.25 * mm});
            skCircle(sketch, "E95.0", {"center": v(29.9, -11) * mm, "radius": 2.25 * mm});
            skCircle(sketch, "E96.0", {"center": v(29.9, 11) * mm, "radius": 2.25 * mm});
            skCircle(sketch, "E97.0", {"center": v(51.9, 11) * mm, "radius": 2.25 * mm});
            skLineSegment(sketch, "E98", {"start": v(-57.15, 16.25) * mm, "end": v(-57.15, -16.25) * mm});
            skLineSegment(sketch, "E99", {"start": v(-57.15, -16.25) * mm, "end": v(-24.65, -16.25) * mm});
            skLineSegment(sketch, "E100", {"start": v(-24.65, -16.25) * mm, "end": v(-24.65, 14.25) * mm});
            skLineSegment(sketch, "E101", {"start": v(0, 0) * mm, "end": v(0, 20) * mm, "construction": true});
            skLineSegment(sketch, "E102", {"start": v(-24.65, 14.25) * mm, "end": v(-19.22, 20) * mm});
            skLineSegment(sketch, "E103", {"start": v(-19.22, 20) * mm, "end": v(0, 20) * mm});
            skLineSegment(sketch, "E104.MirrorCS", {"start": v(19.22, 20) * mm, "end": v(0, 20) * mm});
            skLineSegment(sketch, "E105.MirrorCS", {"start": v(24.65, 14.25) * mm, "end": v(19.22, 20) * mm});
            skLineSegment(sketch, "E106.MirrorCS", {"start": v(24.65, -16.25) * mm, "end": v(24.65, 14.25) * mm});
            skLineSegment(sketch, "E107.MirrorCS", {"start": v(57.15, -16.25) * mm, "end": v(24.65, -16.25) * mm});
            skLineSegment(sketch, "E108.MirrorCS", {"start": v(57.15, 16.25) * mm, "end": v(57.15, -16.25) * mm});
            skLineSegment(sketch, "E109", {"start": v(-57.15, 16.25) * mm, "end": v(-57.15, 16.25) * mm});
            skLineSegment(sketch, "E110", {"start": v(-57.15, 16.25) * mm, "end": v(-30, 45) * mm});
            skLineSegment(sketch, "E111", {"start": v(-30, 45) * mm, "end": v(0, 45) * mm});
            skLineSegment(sketch, "E112.MirrorCS", {"start": v(30, 45) * mm, "end": v(0, 45) * mm});
            skLineSegment(sketch, "E113.MirrorCS", {"start": v(57.15, 16.25) * mm, "end": v(30, 45) * mm});
            skLineSegment(sketch, "E114.MirrorCS", {"start": v(57.15, 16.25) * mm, "end": v(57.15, 16.25) * mm});
            skLineSegment(sketch, "E115", {"start": v(-15.46, 23.98) * mm, "end": v(-33.64, 41.14) * mm, "construction": true});
            skLineSegment(sketch, "E116", {"start": v(0, 20) * mm, "end": v(0, 45) * mm, "construction": true});
            skSolve(sketch);
        }
        {
            var Q0;
            Q0 = qSketchRegion(id + "F19", true);
            extrude(context, id + "F20", {"entities" : qUnion([Q0]), "depth" : 3 * mm, "offsetDistance" : 25 * mm});
        }
        {
            var Q0;
            Q0=makeQuery(id+"F18.opFillet","BLEND_EDGE",EDGE,{"blendedFrom":[makeQuery(id+"F14.opExtrude","SWEPT_EDGE",EDGE,{"disambiguationData":[OSD([sQuery(id+"F13.wireOp",EDGE,"E78.0.7"),sQuery(id+"F13.wireOp",EDGE,"E84")])]}),makeQuery(id+"F14.opExtrude","SWEPT_FACE",FACE,{"disambiguationData":[OSD([sQuery(id+"F13.wireOp",EDGE,"E78.0.6")])]})],"blendedInto":[makeQuery(id+"F14.opExtrude","SWEPT_FACE",FACE,{"disambiguationData":[OSD([sQuery(id+"F13.wireOp",EDGE,"E78.0.6")])]})]});
            var Q1;
            Q1=makeQuery(id+"F18.opFillet","BLEND_EDGE",EDGE,{"blendedFrom":[makeQuery(id+"F14.opExtrude","SWEPT_EDGE",EDGE,{"disambiguationData":[OSD([sQuery(id+"F13.wireOp",EDGE,"E78.0.3"),sQuery(id+"F13.wireOp",EDGE,"E78.0.4")])]}),makeQuery(id+"F14.opExtrude","SWEPT_FACE",FACE,{"disambiguationData":[OSD([sQuery(id+"F13.wireOp",EDGE,"E85.trimOffspring")])]})],"blendedInto":[makeQuery(id+"F14.opExtrude","SWEPT_FACE",FACE,{"disambiguationData":[OSD([sQuery(id+"F13.wireOp",EDGE,"E85.trimOffspring")])]})]});
            fillet(context, id + "F21", {"entities" : qUnion([Q0, Q1]), "radius" : 2 * mm, "tangentPropagation" : true, "allowEdgeOverflow" : false});
        }
        {
            var Q0;
            Q0=makeQuery(id+"F14.opExtrude","CAP_FACE",FACE,{"disambiguationData":[OSD([sQuery(id+"F13.wireOp",EDGE,"E78.0.3"),sQuery(id+"F13.wireOp",EDGE,"E78.0.4"),sQuery(id+"F13.wireOp",EDGE,"E78.0.5"),sQuery(id+"F13.wireOp",EDGE,"E78.0.6"),sQuery(id+"F13.wireOp",EDGE,"E78.0.7"),sQuery(id+"F13.wireOp",EDGE,"E78.0.9"),sQuery(id+"F13.wireOp",EDGE,"E78.0.10"),sQuery(id+"F13.wireOp",EDGE,"E78.0.11"),sQuery(id+"F13.wireOp",EDGE,"E78.0.12"),sQuery(id+"F13.wireOp",EDGE,"E79.0"),sQuery(id+"F13.wireOp",EDGE,"E80.0"),sQuery(id+"F13.wireOp",EDGE,"E81.0"),sQuery(id+"F13.wireOp",EDGE,"E82.0"),sQuery(id+"F13.wireOp",EDGE,"E83.0"),sQuery(id+"F13.wireOp",EDGE,"E84"),sQuery(id+"F13.wireOp",EDGE,"E85.trimOffspring")])],"isStart":true});
            var sketch = newSketch(context, id + "F22", { "sketchPlane" : qUnion([Q0])});
            skCircle(sketch, "E117.cCircle", {"center": v(-29.9, 11) * mm, "radius": 3.5 * mm, "construction": true});
            skLineSegment(sketch, "E117.0", {"start": v(-29.9, 15.04) * mm, "end": v(-26.4, 13.02) * mm});
            skLineSegment(sketch, "E117.1", {"start": v(-26.4, 13.02) * mm, "end": v(-26.4, 8.98) * mm});
            skLineSegment(sketch, "E117.2", {"start": v(-26.4, 8.98) * mm, "end": v(-29.9, 6.96) * mm});
            skLineSegment(sketch, "E117.3", {"start": v(-29.9, 6.96) * mm, "end": v(-33.4, 8.98) * mm});
            skLineSegment(sketch, "E117.4", {"start": v(-33.4, 8.98) * mm, "end": v(-33.4, 13.02) * mm});
            skLineSegment(sketch, "E117.5", {"start": v(-33.4, 13.02) * mm, "end": v(-29.9, 15.04) * mm});
            skPoint(sketch, "E117.0.midPoint", {"position": v(-28.15, 14.03) * mm});
            skSolve(sketch);
        }
        {
            var Q0;
            Q0=makeQuery(id+"F22.imprint","IMPRINT",FACE,{"disambiguationData":[TD([[makeQuery(id+"F22.imprint","IMPRINT",EDGE,{"derivedFrom":sQuery(id+"F22.wireOp",EDGE,"E117.0")}),-1.0]])]});
            extrude(context, id + "F23", {"entities" : qUnion([Q0]), "operationType" : NewBodyOperationType.REMOVE, "oppositeDirection" : true, "depth" : 3 * mm, "offsetDistance" : 25 * mm});
        }
        {
            var Q0;
            Q0=makeQuery(id+"F11.opExtrude","CAP_FACE",FACE,{"disambiguationData":[OSD([sQuery(id+"F10.wireOp",EDGE,"E50"),sQuery(id+"F10.wireOp",EDGE,"E52"),sQuery(id+"F10.wireOp",EDGE,"E53.MirrorCS"),sQuery(id+"F10.wireOp",EDGE,"E54.bottom"),sQuery(id+"F10.wireOp",EDGE,"E54.top"),sQuery(id+"F10.wireOp",EDGE,"E54.left"),sQuery(id+"F10.wireOp",EDGE,"E54.right"),sQuery(id+"F10.wireOp",EDGE,"E55"),sQuery(id+"F10.wireOp",EDGE,"E56"),sQuery(id+"F10.wireOp",EDGE,"E57"),sQuery(id+"F10.wireOp",EDGE,"E58"),sQuery(id+"F10.wireOp",EDGE,"E59"),sQuery(id+"F10.wireOp",EDGE,"E63.trimOffspring"),sQuery(id+"F10.wireOp",EDGE,"E66.0"),sQuery(id+"F10.wireOp",EDGE,"E67.0"),sQuery(id+"F10.wireOp",EDGE,"E68.0"),sQuery(id+"F10.wireOp",EDGE,"E69.0"),sQuery(id+"F10.wireOp",EDGE,"E70"),sQuery(id+"F10.wireOp",EDGE,"E71"),sQuery(id+"F10.wireOp",EDGE,"E72"),sQuery(id+"F10.wireOp",EDGE,"E73.trimOffspring")])],"isStart":false});
            var sketch = newSketch(context, id + "F24", { "sketchPlane" : qUnion([Q0])});
            skCircle(sketch, "E118.0", {"center": v(-29.9, -11) * mm, "radius": 2.37 * mm, "construction": true});
            skCircle(sketch, "E119", {"center": v(-29.9, -11) * mm, "radius": 3.5 * mm});
            skSolve(sketch);
        }
        {
            var Q0;
            Q0 = qSketchRegion(id + "F24", true);
            extrude(context, id + "F25", {"entities" : qUnion([Q0]), "operationType" : NewBodyOperationType.REMOVE, "oppositeDirection" : true, "depth" : 25 * mm, "offsetDistance" : 25 * mm, "hasDraft" : true, "draftAngle" : 45 * degree, "draftPullDirection" : true});
        }
        {
            var Q0;
            {var subQ0=sQuery(id+"F10.wireOp",EDGE,"E58");var subQ1=sQuery(id+"F10.wireOp",EDGE,"E72");var subQ2=sQuery(id+"F10.wireOp",EDGE,"E56");var subQ3=sQuery(id+"F10.wireOp",EDGE,"E55");var subQ5=sQuery(id+"F10.wireOp",EDGE,"E57");var subQ6=sQuery(id+"F10.wireOp",EDGE,"E50");var subQ7=sQuery(id+"F10.wireOp",EDGE,"E52");var subQ8=sQuery(id+"F10.wireOp",EDGE,"E68.0");var subQ9=sQuery(id+"F10.wireOp",EDGE,"E54.top");var subQ10=sQuery(id+"F10.wireOp",EDGE,"E54.left");Q0=makeQuery(id+"F15.boolean.opBoolean","SPLIT",FACE,{"disambiguationData":[TD([makeQuery(id+"F11.opExtrude","SWEPT_FACE",FACE,{"disambiguationData":[OSD([subQ7])]})])],"derivedFrom":makeQuery(id+"F11.opExtrude","CAP_FACE",FACE,{"disambiguationData":[OSD([subQ6,subQ7,sQuery(id+"F10.wireOp",EDGE,"E53.MirrorCS"),sQuery(id+"F10.wireOp",EDGE,"E54.bottom"),subQ9,subQ10,sQuery(id+"F10.wireOp",EDGE,"E54.right"),subQ3,subQ2,subQ5,subQ0,sQuery(id+"F10.wireOp",EDGE,"E59"),sQuery(id+"F10.wireOp",EDGE,"E63.trimOffspring"),sQuery(id+"F10.wireOp",EDGE,"E66.0"),sQuery(id+"F10.wireOp",EDGE,"E67.0"),subQ8,sQuery(id+"F10.wireOp",EDGE,"E69.0"),sQuery(id+"F10.wireOp",EDGE,"E70"),sQuery(id+"F10.wireOp",EDGE,"E71"),subQ1,sQuery(id+"F10.wireOp",EDGE,"E73.trimOffspring")])],"isStart":true})});}
            var sketch = newSketch(context, id + "F26", { "sketchPlane" : qUnion([Q0])});
            skLineSegment(sketch, "E120.0.0", {"start": v(34.9, -15.46) * mm, "end": v(34.9, -9.86) * mm});
            skArc(sketch, "E120.0.1", {"start": v(34.9, -9.86) * mm, "mid": v(34.7, -9) * mm, "end": v(34.16, -8.31) * mm});
            skArc(sketch, "E120.0.2", {"start": v(34.16, -8.31) * mm, "mid": v(30.3, -1.42) * mm, "end": v(32.22, 6.25) * mm});
            skLineSegment(sketch, "E120.0.3", {"start": v(32.22, 6.25) * mm, "end": v(22.65, 6.25) * mm});
            skLineSegment(sketch, "E120.0.4", {"start": v(22.65, 6.25) * mm, "end": v(22.65, 18.75) * mm});
            skLineSegment(sketch, "E120.0.5", {"start": v(22.65, 18.75) * mm, "end": v(22.15, 18.75) * mm});
            skArc(sketch, "E120.0.6", {"start": v(22.15, 18.75) * mm, "mid": v(20.74, 18.16) * mm, "end": v(20.15, 16.75) * mm});
            skLineSegment(sketch, "E120.0.7", {"start": v(20.15, 16.75) * mm, "end": v(20.15, 4.1) * mm});
            skArc(sketch, "E120.0.8", {"start": v(20.15, 4.1) * mm, "mid": v(20.18, 3.76) * mm, "end": v(20.27, 3.42) * mm});
            skLineSegment(sketch, "E120.0.9", {"start": v(20.27, 3.42) * mm, "end": v(23.61, -5.71) * mm});
            skArc(sketch, "E120.0.10", {"start": v(23.61, -5.71) * mm, "mid": v(23.73, -6.56) * mm, "end": v(23.47, -7.38) * mm});
            skArc(sketch, "E120.0.11", {"start": v(23.47, -7.38) * mm, "mid": v(24.9, -16.42) * mm, "end": v(34.02, -17.12) * mm});
            skArc(sketch, "E120.0.12", {"start": v(34.02, -17.12) * mm, "mid": v(34.67, -16.4) * mm, "end": v(34.9, -15.46) * mm});
            skCircle(sketch, "E121.0", {"center": v(29.9, -11) * mm, "radius": 2.37 * mm});
            skCircle(sketch, "E122.0", {"center": v(29.9, 11) * mm, "radius": 2.37 * mm});
            skLineSegment(sketch, "E123.0.0", {"start": v(41.6, 18.19) * mm, "end": v(27.19, 18.75) * mm});
            skArc(sketch, "E123.0.1", {"start": v(27.19, 18.75) * mm, "mid": v(27.15, 18.75) * mm, "end": v(27.11, 18.75) * mm});
            skLineSegment(sketch, "E123.0.2", {"start": v(27.11, 18.75) * mm, "end": v(22.65, 18.75) * mm});
            skLineSegment(sketch, "E123.0.4", {"start": v(22.65, 16.25) * mm, "end": v(24.65, 16.25) * mm});
            skLineSegment(sketch, "E123.0.5", {"start": v(24.65, 16.25) * mm, "end": v(24.65, 6.25) * mm});
            skLineSegment(sketch, "E123.0.6", {"start": v(24.65, 6.25) * mm, "end": v(32.22, 6.25) * mm});
            skArc(sketch, "E123.0.7", {"start": v(32.22, 6.25) * mm, "mid": v(40.9, 10.7) * mm, "end": v(49.58, 6.25) * mm});
            skLineSegment(sketch, "E123.0.8", {"start": v(49.58, 6.25) * mm, "end": v(58.07, 6.25) * mm});
            skArc(sketch, "E123.0.9", {"start": v(58.07, 6.25) * mm, "mid": v(58.11, 6.83) * mm, "end": v(58.32, 7.37) * mm});
            skArc(sketch, "E123.0.10", {"start": v(58.32, 7.37) * mm, "mid": v(57.11, 16.21) * mm, "end": v(48.27, 17.42) * mm});
            skArc(sketch, "E123.0.11", {"start": v(48.27, 17.42) * mm, "mid": v(47.48, 17.17) * mm, "end": v(46.66, 17.27) * mm});
            skArc(sketch, "E123.0.12", {"start": v(46.66, 17.27) * mm, "mid": v(44.17, 17.9) * mm, "end": v(41.6, 18.19) * mm});
            skLineSegment(sketch, "E124.0.0", {"start": v(46.9, -9.86) * mm, "end": v(46.9, -15.46) * mm});
            skArc(sketch, "E124.0.1", {"start": v(46.9, -15.46) * mm, "mid": v(47.13, -16.4) * mm, "end": v(47.78, -17.12) * mm});
            skArc(sketch, "E124.0.2", {"start": v(47.78, -17.12) * mm, "mid": v(56.9, -16.41) * mm, "end": v(58.32, -7.37) * mm});
            skArc(sketch, "E124.0.3", {"start": v(58.32, -7.37) * mm, "mid": v(58.07, -6.58) * mm, "end": v(58.17, -5.76) * mm});
            skArc(sketch, "E124.0.4", {"start": v(58.17, -5.76) * mm, "mid": v(59.1, 0) * mm, "end": v(58.17, 5.76) * mm});
            skArc(sketch, "E124.0.5", {"start": v(58.17, 5.76) * mm, "mid": v(58.1, 6) * mm, "end": v(58.07, 6.25) * mm});
            skLineSegment(sketch, "E124.0.6", {"start": v(58.07, 6.25) * mm, "end": v(49.58, 6.25) * mm});
            skArc(sketch, "E124.0.7", {"start": v(49.58, 6.25) * mm, "mid": v(51.5, -1.42) * mm, "end": v(47.64, -8.31) * mm});
            skArc(sketch, "E124.0.8", {"start": v(47.64, -8.31) * mm, "mid": v(47.1, -9) * mm, "end": v(46.9, -9.86) * mm});
            skCircle(sketch, "E125.0", {"center": v(51.9, 11) * mm, "radius": 2.38 * mm});
            skCircle(sketch, "E126.0", {"center": v(51.9, -11) * mm, "radius": 2.38 * mm});
            skSolve(sketch);
        }
        {
            var Q0;
            Q0 = qSketchRegion(id + "F26", true);
            extrude(context, id + "F27", {"entities" : qUnion([Q0]), "depth" : 25 * mm, "offsetDistance" : 25 * mm});
        }
    });
